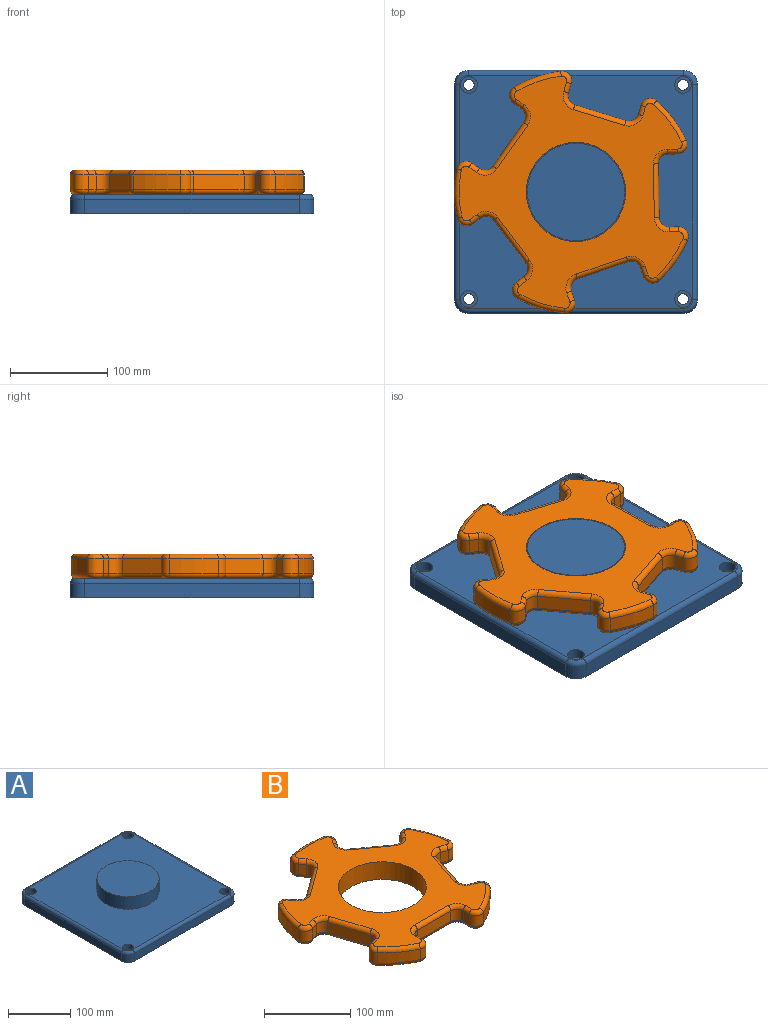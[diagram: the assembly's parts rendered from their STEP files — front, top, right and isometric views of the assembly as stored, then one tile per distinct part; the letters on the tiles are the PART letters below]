
ASSEMBLY  parts=2 mates=1
PART A: 32 faces, bbox 252.5x252.5x45 mm
  f0: plane 220x15mm, normal (1,0,0), area 3300mm2, adj f5,f8,f11,f27
  f1: plane 220x15mm, normal (0,1,0), area 3300mm2, adj f5,f8,f9,f31
  f2: plane 220x15mm, normal (-1,0,0), area 3300mm2, adj f5,f9,f10,f28
  f3: plane 220x15mm, normal (0,-1,0), area 3300mm2, adj f5,f10,f11,f24
  f4: plane 240x240mm, normal (0,0,1), area 48725.4mm2, adj f6,f14,f17,f20,f23,f24,f25,f26
  f5: plane 250x250mm, normal (0,0,-1), area 61926.7mm2, adj f0,f1,f2,f3,f8,f9,f10,f11
  f6: cylinder r=50mm len=100mm, axis (0,0,-1), area 7854mm2, adj f4,f7
  f7: plane 100x100mm, normal (0,0,1), area 7854mm2, adj f6
  f8: cylinder r=15mm len=15mm, axis (0,0,-1), area 353.4mm2, adj f0,f1,f5,f29
  f9: cylinder r=15mm len=15mm, axis (0,0,1), area 353.4mm2, adj f1,f2,f5,f30
  f10: cylinder r=15mm len=15mm, axis (0,0,-1), area 353.4mm2, adj f2,f3,f5,f26
  f11: cylinder r=15mm len=15mm, axis (0,0,1), area 353.4mm2, adj f0,f3,f5,f25
  f12: cylinder r=5.5mm len=11mm, axis (0,0,1), area 345.6mm2, adj f5,f13
  f13: plane 17.25x17.25mm, normal (0,0,1), area 138.7mm2, adj f12,f14
  f14: cylinder r=8.62mm len=17.25mm, axis (0,0,1), area 541.9mm2, adj f4,f13
  f15: cylinder r=5.5mm len=11mm, axis (0,0,1), area 345.6mm2, adj f5,f16
  f16: plane 17.25x17.25mm, normal (0,0,1), area 138.7mm2, adj f15,f17
  f17: cylinder r=8.62mm len=17.25mm, axis (0,0,1), area 541.9mm2, adj f4,f16
  f18: cylinder r=5.5mm len=11mm, axis (0,0,1), area 345.6mm2, adj f5,f19
  f19: plane 17.25x17.25mm, normal (0,0,1), area 138.7mm2, adj f18,f20
  f20: cylinder r=8.62mm len=17.25mm, axis (0,0,1), area 541.9mm2, adj f4,f19
  f21: cylinder r=5.5mm len=11mm, axis (0,0,1), area 345.6mm2, adj f5,f22
  f22: plane 17.25x17.25mm, normal (0,0,1), area 138.7mm2, adj f21,f23
  f23: cylinder r=8.62mm len=17.25mm, axis (0,0,1), area 541.9mm2, adj f4,f22
  f24: cylinder r=5mm len=220mm, axis (-1,0,0), area 1727.9mm2, adj f3,f4,f25,f26
  f25: torus R=10mm, axis (0,0,1), area 162.6mm2, adj f4,f11,f24,f27
  f26: torus R=10mm, axis (0,0,1), area 162.6mm2, adj f4,f10,f24,f28
  f27: cylinder r=5mm len=220mm, axis (0,-1,0), area 1727.9mm2, adj f0,f4,f25,f29
  f28: cylinder r=5mm len=220mm, axis (0,1,0), area 1727.9mm2, adj f2,f4,f26,f30
  f29: torus R=10mm, axis (0,0,1), area 162.6mm2, adj f4,f8,f27,f31
  f30: torus R=10mm, axis (0,0,1), area 162.6mm2, adj f4,f9,f28,f31
  f31: cylinder r=5mm len=220mm, axis (1,0,0), area 1727.9mm2, adj f1,f4,f29,f30
PART B: 123 faces, bbox 268.9x258.5x25 mm
  f0: plane 238.57x229.73mm, normal (0,0,1), area 21505.7mm2, adj f6,f43,f44,f45,f46,f47,f48,f49
  f1: plane 238.57x229.73mm, normal (0,0,-1), area 21505.7mm2, adj f6,f83,f84,f85,f86,f87,f88,f89
  f2: cylinder r=125mm len=40.68mm, axis (0,0,-1), area 759.5mm2, adj f13,f42,f51,f91
  f3: cylinder r=125mm len=47.82mm, axis (0,0,-1), area 759.5mm2, adj f35,f41,f67,f107
  f4: cylinder r=125mm len=50.29mm, axis (0,0,-1), area 759.5mm2, adj f28,f34,f82,f122
  f5: cylinder r=125mm len=47.82mm, axis (0,0,-1), area 759.5mm2, adj f21,f27,f66,f106
  f6: cylinder r=51mm len=102mm, axis (0,0,-1), area 8011.1mm2, adj f0,f1
  f7: cylinder r=125mm len=40.68mm, axis (0,0,-1), area 759.5mm2, adj f14,f20,f50,f90
  f8: plane 15x9.73mm, normal (-1,0,0), area 146mm2, adj f11,f14,f46,f86
  f9: plane 55x15mm, normal (0,-1,0), area 825mm2, adj f11,f12,f43,f83
  f10: plane 15x9.73mm, normal (1,0,0), area 146mm2, adj f12,f13,f47,f87
  f11: cylinder r=10mm len=15mm, axis (0,0,-1), area 235.6mm2, adj f8,f9,f44,f84
  f12: cylinder r=10mm len=15mm, axis (0,0,-1), area 235.6mm2, adj f9,f10,f45,f85
  f13: cylinder r=10mm len=15mm, axis (0,0,-1), area 299.5mm2, adj f2,f10,f49,f89
  f14: cylinder r=10mm len=15mm, axis (0,0,-1), area 299.5mm2, adj f7,f8,f48,f88
  f15: plane 15x9.26mm, normal (-0.31,-0.95,0), area 146mm2, adj f18,f21,f62,f102
  f16: plane 52.31x17mm, normal (0.95,-0.31,0), area 825mm2, adj f18,f19,f58,f98
  f17: plane 15x9.26mm, normal (0.31,0.95,0), area 146mm2, adj f19,f20,f54,f94
  f18: cylinder r=10mm len=15mm, axis (0,0,-1), area 235.6mm2, adj f15,f16,f60,f100
  f19: cylinder r=10mm len=15mm, axis (0,0,-1), area 235.6mm2, adj f16,f17,f56,f96
  f20: cylinder r=10mm len=16.25mm, axis (0,0,-1), area 299.5mm2, adj f7,f17,f52,f92
  f21: cylinder r=10mm len=15mm, axis (0,0,-1), area 299.5mm2, adj f5,f15,f64,f104
  f22: plane 15x7.87mm, normal (0.81,-0.59,0), area 146mm2, adj f25,f28,f78,f118
  f23: plane 44.5x32.33mm, normal (0.59,0.81,0), area 825mm2, adj f25,f26,f74,f114
  f24: plane 15x7.87mm, normal (-0.81,0.59,0), area 146mm2, adj f26,f27,f70,f110
  f25: cylinder r=10mm len=15mm, axis (0,0,-1), area 235.6mm2, adj f22,f23,f76,f116
  f26: cylinder r=10mm len=15mm, axis (0,0,-1), area 235.6mm2, adj f23,f24,f72,f112
  f27: cylinder r=10mm len=16.78mm, axis (0,0,-1), area 299.5mm2, adj f5,f24,f68,f108
  f28: cylinder r=10mm len=15.67mm, axis (0,0,-1), area 299.5mm2, adj f4,f22,f80,f120
  f29: plane 15x7.87mm, normal (0.81,0.59,0), area 146mm2, adj f32,f35,f71,f111
  f30: plane 44.5x32.33mm, normal (-0.59,0.81,0), area 825mm2, adj f32,f33,f75,f115
  f31: plane 15x7.87mm, normal (-0.81,-0.59,0), area 146mm2, adj f33,f34,f79,f119
  f32: cylinder r=10mm len=15mm, axis (0,0,-1), area 235.6mm2, adj f29,f30,f73,f113
  f33: cylinder r=10mm len=15mm, axis (0,0,-1), area 235.6mm2, adj f30,f31,f77,f117
  f34: cylinder r=10mm len=15.67mm, axis (0,0,-1), area 299.5mm2, adj f4,f31,f81,f121
  f35: cylinder r=10mm len=16.78mm, axis (0,0,-1), area 299.5mm2, adj f3,f29,f69,f109
  f36: plane 15x9.26mm, normal (-0.31,0.95,0), area 146mm2, adj f39,f42,f55,f95
  f37: plane 52.31x17mm, normal (-0.95,-0.31,0), area 825mm2, adj f39,f40,f59,f99
  f38: plane 15x9.26mm, normal (0.31,-0.95,0), area 146mm2, adj f40,f41,f63,f103
  f39: cylinder r=10mm len=15mm, axis (0,0,-1), area 235.6mm2, adj f36,f37,f57,f97
  f40: cylinder r=10mm len=15mm, axis (0,0,-1), area 235.6mm2, adj f37,f38,f61,f101
  f41: cylinder r=10mm len=15mm, axis (0,0,-1), area 299.5mm2, adj f3,f38,f65,f105
  f42: cylinder r=10mm len=16.25mm, axis (0,0,-1), area 299.5mm2, adj f2,f36,f53,f93
  f43: cylinder r=5mm len=55mm, axis (1,0,0), area 432mm2, adj f0,f9,f44,f45
  f44: torus R=15mm, axis (0,0,1), area 145.8mm2, adj f0,f11,f43,f46
  f45: torus R=15mm, axis (0,0,1), area 145.8mm2, adj f0,f12,f43,f47
  f46: cylinder r=5mm len=9.73mm, axis (0,-1,0), area 76.4mm2, adj f0,f8,f44,f48
  f47: cylinder r=5mm len=9.73mm, axis (0,1,0), area 76.4mm2, adj f0,f10,f45,f49
  f48: torus R=5mm, axis (0,0,1), area 128.3mm2, adj f0,f14,f46,f50
  f49: torus R=5mm, axis (0,0,1), area 128.3mm2, adj f0,f13,f47,f51
  f50: torus R=120mm, axis (0,0,1), area 391.9mm2, adj f0,f7,f48,f52
  f51: torus R=120mm, axis (0,0,1), area 391.9mm2, adj f0,f2,f49,f53
  f52: torus R=5mm, axis (0,0,1), area 128.3mm2, adj f0,f20,f50,f54
  f53: torus R=5mm, axis (0,0,1), area 128.3mm2, adj f0,f42,f51,f55
  f54: cylinder r=5mm len=10.8mm, axis (-0.95,0.31,0), area 76.4mm2, adj f0,f17,f52,f56
  f55: cylinder r=5mm len=10.8mm, axis (-0.95,-0.31,0), area 76.4mm2, adj f0,f36,f53,f57
  f56: torus R=15mm, axis (0,0,1), area 145.8mm2, adj f0,f19,f54,f58
  f57: torus R=15mm, axis (0,0,1), area 145.8mm2, adj f0,f39,f55,f59
  f58: cylinder r=5mm len=53.85mm, axis (0.31,0.95,0), area 432mm2, adj f0,f16,f56,f60
  f59: cylinder r=5mm len=53.85mm, axis (0.31,-0.95,0), area 432mm2, adj f0,f37,f57,f61
  f60: torus R=15mm, axis (0,0,1), area 145.8mm2, adj f0,f18,f58,f62
  f61: torus R=15mm, axis (0,0,1), area 145.8mm2, adj f0,f40,f59,f63
  f62: cylinder r=5mm len=10.8mm, axis (0.95,-0.31,0), area 76.4mm2, adj f0,f15,f60,f64
  f63: cylinder r=5mm len=10.8mm, axis (0.95,0.31,0), area 76.4mm2, adj f0,f38,f61,f65
  f64: torus R=5mm, axis (0,0,1), area 128.3mm2, adj f0,f21,f62,f66
  f65: torus R=5mm, axis (0,0,1), area 128.3mm2, adj f0,f41,f63,f67
  f66: torus R=120mm, axis (0,0,1), area 391.9mm2, adj f0,f5,f64,f68
  f67: torus R=120mm, axis (0,0,1), area 391.9mm2, adj f0,f3,f65,f69
  f68: torus R=5mm, axis (0,0,1), area 128.3mm2, adj f0,f27,f66,f70
  f69: torus R=5mm, axis (0,0,1), area 128.3mm2, adj f0,f35,f67,f71
  f70: cylinder r=5mm len=10.81mm, axis (-0.59,-0.81,0), area 76.4mm2, adj f0,f24,f68,f72
  f71: cylinder r=5mm len=10.81mm, axis (-0.59,0.81,0), area 76.4mm2, adj f0,f29,f69,f73
  f72: torus R=15mm, axis (0,0,1), area 145.8mm2, adj f0,f26,f70,f74
  f73: torus R=15mm, axis (0,0,1), area 145.8mm2, adj f0,f32,f71,f75
  f74: cylinder r=5mm len=47.44mm, axis (-0.81,0.59,0), area 432mm2, adj f0,f23,f72,f76
  f75: cylinder r=5mm len=47.44mm, axis (-0.81,-0.59,0), area 432mm2, adj f0,f30,f73,f77
  f76: torus R=15mm, axis (0,0,1), area 145.8mm2, adj f0,f25,f74,f78
  f77: torus R=15mm, axis (0,0,1), area 145.8mm2, adj f0,f33,f75,f79
  f78: cylinder r=5mm len=10.81mm, axis (0.59,0.81,0), area 76.4mm2, adj f0,f22,f76,f80
  f79: cylinder r=5mm len=10.81mm, axis (0.59,-0.81,0), area 76.4mm2, adj f0,f31,f77,f81
  f80: torus R=5mm, axis (0,0,1), area 128.3mm2, adj f0,f28,f78,f82
  f81: torus R=5mm, axis (0,0,1), area 128.3mm2, adj f0,f34,f79,f82
  f82: torus R=120mm, axis (0,0,1), area 391.9mm2, adj f0,f4,f80,f81
  f83: cylinder r=5mm len=55mm, axis (-1,0,0), area 432mm2, adj f1,f9,f84,f85
  f84: torus R=15mm, axis (0,0,1), area 145.8mm2, adj f1,f11,f83,f86
  f85: torus R=15mm, axis (0,0,1), area 145.8mm2, adj f1,f12,f83,f87
  f86: cylinder r=5mm len=9.73mm, axis (0,1,0), area 76.4mm2, adj f1,f8,f84,f88
  f87: cylinder r=5mm len=9.73mm, axis (0,-1,0), area 76.4mm2, adj f1,f10,f85,f89
  f88: torus R=5mm, axis (0,0,1), area 128.3mm2, adj f1,f14,f86,f90
  f89: torus R=5mm, axis (0,0,1), area 128.3mm2, adj f1,f13,f87,f91
  f90: torus R=120mm, axis (0,0,1), area 391.9mm2, adj f1,f7,f88,f92
  f91: torus R=120mm, axis (0,0,1), area 391.9mm2, adj f1,f2,f89,f93
  f92: torus R=5mm, axis (0,0,1), area 128.3mm2, adj f1,f20,f90,f94
  f93: torus R=5mm, axis (0,0,1), area 128.3mm2, adj f1,f42,f91,f95
  f94: cylinder r=5mm len=10.8mm, axis (0.95,-0.31,0), area 76.4mm2, adj f1,f17,f92,f96
  f95: cylinder r=5mm len=10.8mm, axis (0.95,0.31,0), area 76.4mm2, adj f1,f36,f93,f97
  f96: torus R=15mm, axis (0,0,1), area 145.8mm2, adj f1,f19,f94,f98
  f97: torus R=15mm, axis (0,0,1), area 145.8mm2, adj f1,f39,f95,f99
  f98: cylinder r=5mm len=53.85mm, axis (-0.31,-0.95,0), area 432mm2, adj f1,f16,f96,f100
  f99: cylinder r=5mm len=53.85mm, axis (-0.31,0.95,0), area 432mm2, adj f1,f37,f97,f101
  f100: torus R=15mm, axis (0,0,1), area 145.8mm2, adj f1,f18,f98,f102
  f101: torus R=15mm, axis (0,0,1), area 145.8mm2, adj f1,f40,f99,f103
  f102: cylinder r=5mm len=10.8mm, axis (-0.95,0.31,0), area 76.4mm2, adj f1,f15,f100,f104
  f103: cylinder r=5mm len=10.8mm, axis (-0.95,-0.31,0), area 76.4mm2, adj f1,f38,f101,f105
  f104: torus R=5mm, axis (0,0,1), area 128.3mm2, adj f1,f21,f102,f106
  f105: torus R=5mm, axis (0,0,1), area 128.3mm2, adj f1,f41,f103,f107
  f106: torus R=120mm, axis (0,0,1), area 391.9mm2, adj f1,f5,f104,f108
  f107: torus R=120mm, axis (0,0,1), area 391.9mm2, adj f1,f3,f105,f109
  f108: torus R=5mm, axis (0,0,1), area 128.3mm2, adj f1,f27,f106,f110
  f109: torus R=5mm, axis (0,0,1), area 128.3mm2, adj f1,f35,f107,f111
  f110: cylinder r=5mm len=10.81mm, axis (0.59,0.81,0), area 76.4mm2, adj f1,f24,f108,f112
  f111: cylinder r=5mm len=10.81mm, axis (0.59,-0.81,0), area 76.4mm2, adj f1,f29,f109,f113
  f112: torus R=15mm, axis (0,0,1), area 145.8mm2, adj f1,f26,f110,f114
  f113: torus R=15mm, axis (0,0,1), area 145.8mm2, adj f1,f32,f111,f115
  f114: cylinder r=5mm len=47.44mm, axis (0.81,-0.59,0), area 432mm2, adj f1,f23,f112,f116
  f115: cylinder r=5mm len=47.44mm, axis (0.81,0.59,0), area 432mm2, adj f1,f30,f113,f117
  f116: torus R=15mm, axis (0,0,1), area 145.8mm2, adj f1,f25,f114,f118
  f117: torus R=15mm, axis (0,0,1), area 145.8mm2, adj f1,f33,f115,f119
  f118: cylinder r=5mm len=10.81mm, axis (-0.59,-0.81,0), area 76.4mm2, adj f1,f22,f116,f120
  f119: cylinder r=5mm len=10.81mm, axis (-0.59,0.81,0), area 76.4mm2, adj f1,f31,f117,f121
  f120: torus R=5mm, axis (0,0,1), area 128.3mm2, adj f1,f28,f118,f122
  f121: torus R=5mm, axis (0,0,1), area 128.3mm2, adj f1,f34,f119,f122
  f122: torus R=120mm, axis (0,0,1), area 391.9mm2, adj f1,f4,f120,f121
PLACE A at identity fixed
PLACE B rot(axis=(0,0,1),18.8deg) t=(0,0,0)mm
MATE revolute B.f2 <-> A.f6  axis (0,0,-1) through (0,0,32.5)mm
